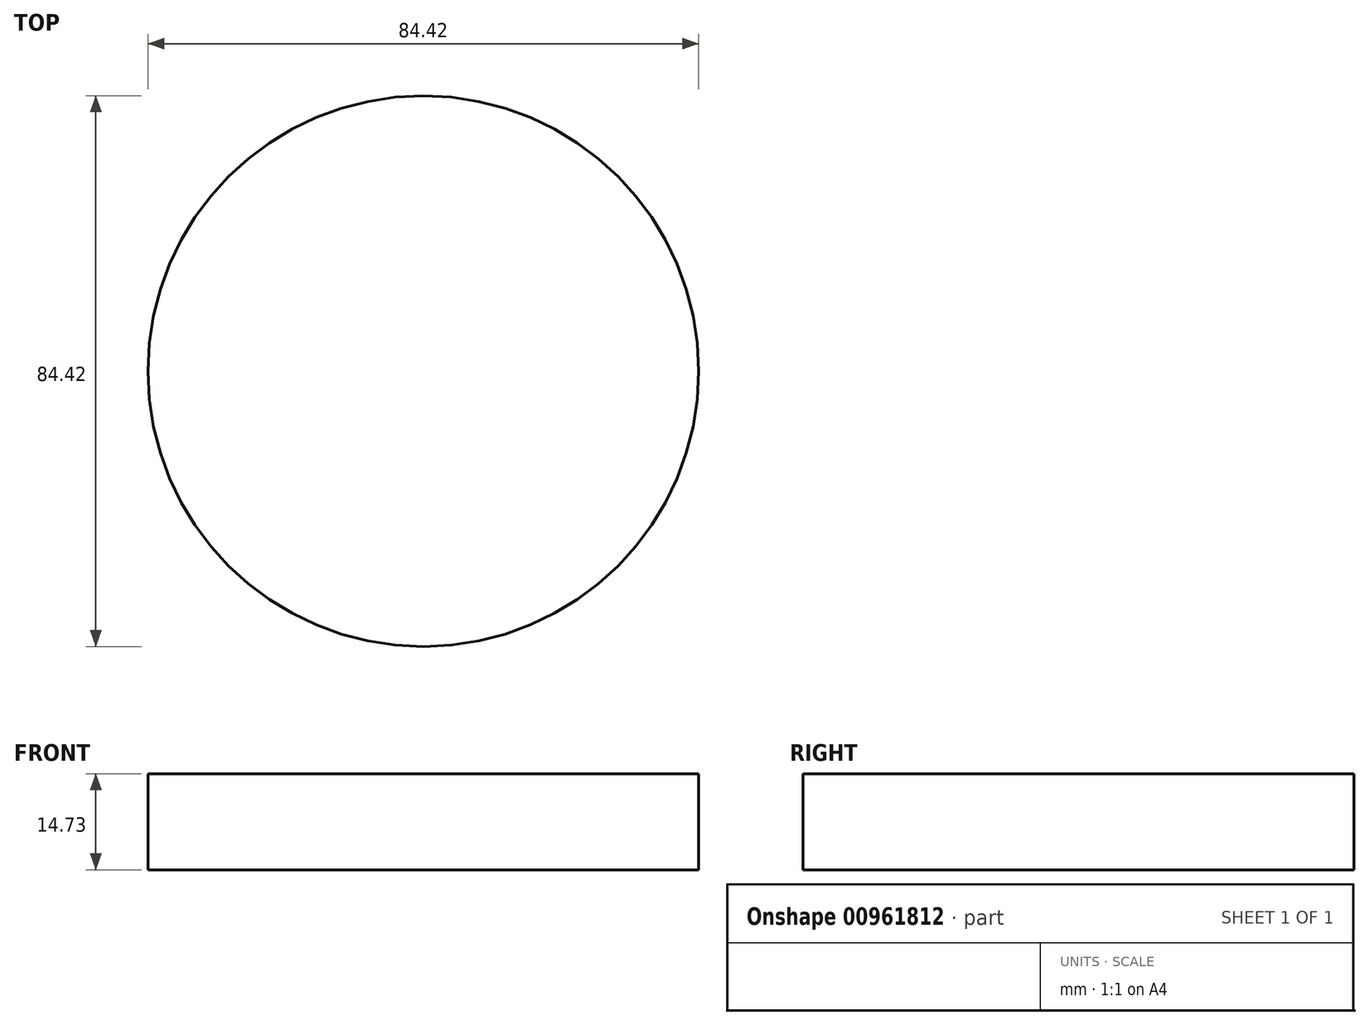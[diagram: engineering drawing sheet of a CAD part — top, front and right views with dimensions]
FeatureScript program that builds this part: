
annotation { "Feature Type Name" : "Feature", "Feature Type Description" : "" }
export const myFeature = defineFeature(function(context is Context, id is Id, definition is map)
    precondition{}
    {
        {
            var Q0;
            Q0=qCreatedBy(makeId("Top.planeOp"),FACE);
            var sketch = newSketch(context, id + "F0", { "sketchPlane" : qUnion([Q0])});
            skCircle(sketch, "E0", {"center": v(0, 0) * mm, "radius": 42.21 * mm});
            skSolve(sketch);
        }
        {
            var Q0;
            Q0 = qSketchRegion(id + "F0", true);
            extrude(context, id + "F1", {"entities" : qUnion([Q0]), "depth" : 14.73 * mm, "offsetDistance" : 25.4 * mm});
        }
    });
